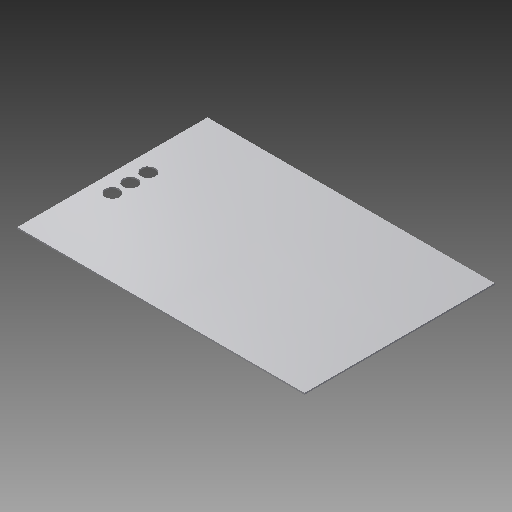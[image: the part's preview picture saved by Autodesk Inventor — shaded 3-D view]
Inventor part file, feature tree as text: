
AUTODESK INVENTOR PART (.ipt)
format: ipt  version: 2018 (Build 220112000, 112)  size: 114,176 bytes
history: native  units: mm
features: extrude x1, hole x1
ambient origin geometry x8: Origin, YZ Plane, XZ Plane, XY Plane, X Axis, Y Axis, Z Axis, Center Point
bodies: Volumenkörper1 (feature_tree)
feature tree (2):
  extrude  "Extrusion1"  Depth=800.0mm
  hole  "Bohrung1"  [1 undecoded]
note: 1 required parameter value undecoded (feature->parameter linkage not recoverable at this tier; creation-order binding heuristic only, values carry confidence <= 0.55)
